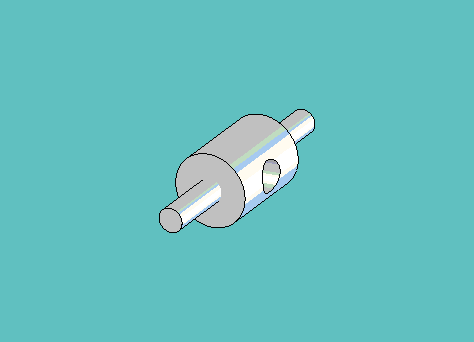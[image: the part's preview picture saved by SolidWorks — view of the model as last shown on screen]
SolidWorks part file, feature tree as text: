
SOLIDWORKS PART (.sldprt)
format: sldprt  version: not decoded by parser v0  size: 232,448 bytes
history: native  units: mm
features: sketch x4, extrude x3, material x1, cut_extrude x1 (+11 scaffold rows collapsed)
feature tree (20):
  scaffold x11  (default folders/planes/origin — collapsed)
  material  "Material <not specified>"
  sketch  "Sketch1"  dims[D1=9.525mm]
  extrude  "Extrude1"  Depth=6.35mm
  sketch  "Sketch2"  dims[D1=4.1148mm]
  cut_extrude  "Cut-Extrude1"  [1 undecoded]
  sketch  "Sketch3"  dims[D1=3.175mm]
  extrude  "Extrude2"  Depth=9.525mm
  sketch  "Sketch4"
  extrude  "Extrude3"  Depth=9.525mm
decode coverage: 6 of 8 modeling features carry decoded parameters
note: 1 parameter value undecoded
note: suppression state not decoded; provenance and decode notes live in map.json
